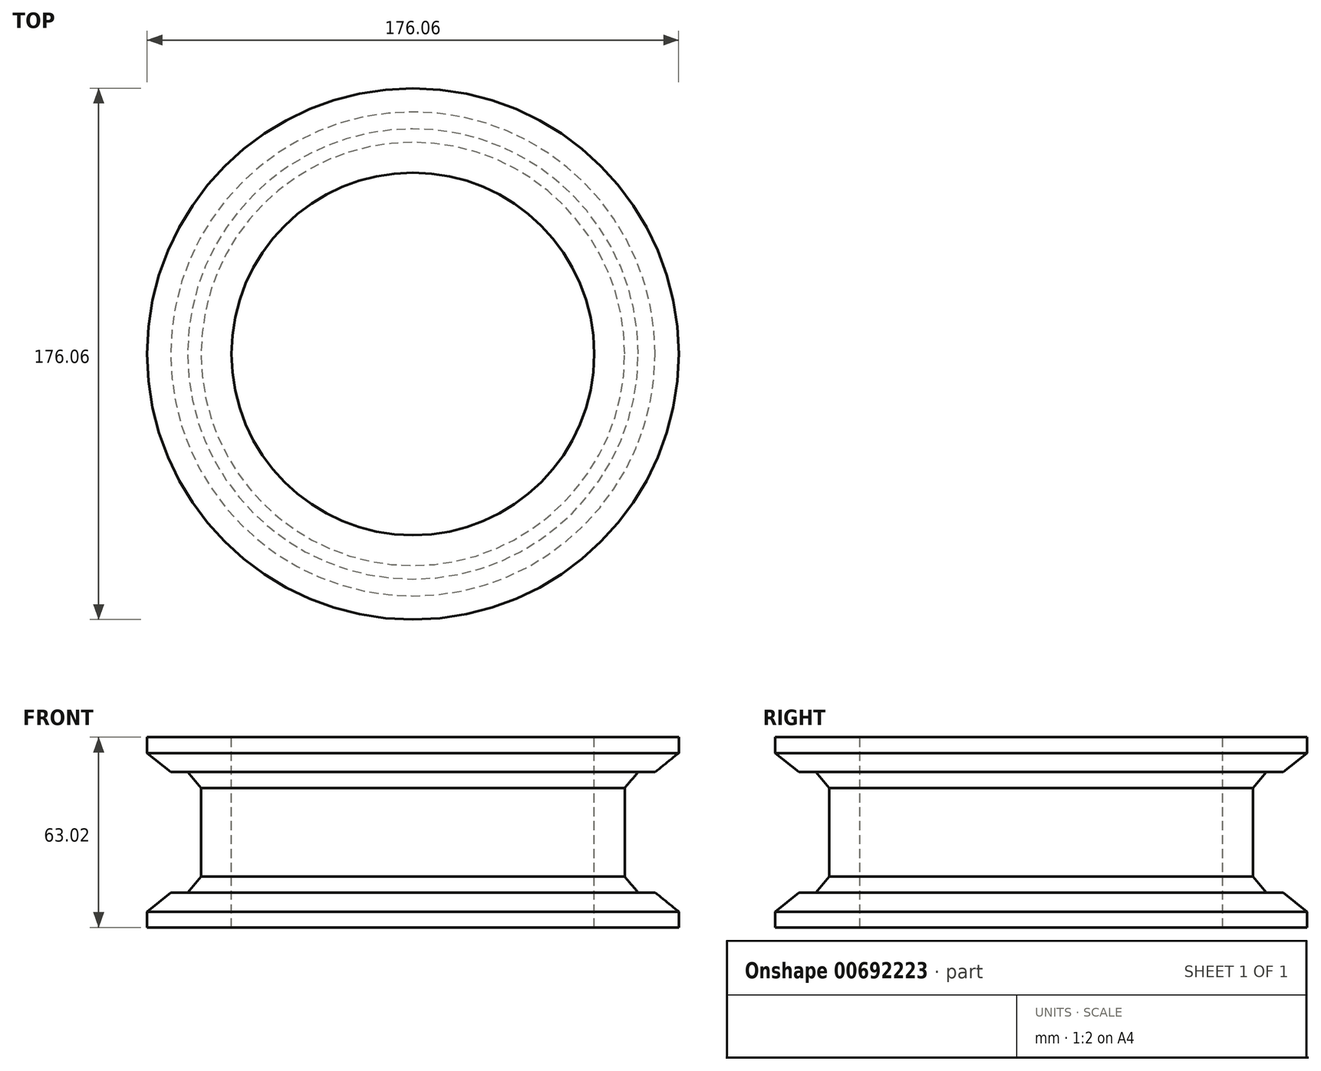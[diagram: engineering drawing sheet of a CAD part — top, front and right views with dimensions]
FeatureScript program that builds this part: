
annotation { "Feature Type Name" : "Feature", "Feature Type Description" : "" }
export const myFeature = defineFeature(function(context is Context, id is Id, definition is map)
    precondition{}
    {
        {
            var Q0;
            Q0=qCreatedBy(makeId("Front.planeOp"),FACE);
            var sketch = newSketch(context, id + "F0", { "sketchPlane" : qUnion([Q0])});
            skLineSegment(sketch, "E0", {"start": v(0, 0) * mm, "end": v(0, -31.5) * mm});
            skLineSegment(sketch, "E1", {"start": v(0, -31.5) * mm, "end": v(-88.03, -31.5) * mm});
            skLineSegment(sketch, "E2", {"start": v(-88.03, -31.5) * mm, "end": v(-88.03, -26.29) * mm});
            skLineSegment(sketch, "E3", {"start": v(-88.03, -26.29) * mm, "end": v(-80.2, -19.95) * mm});
            skLineSegment(sketch, "E4", {"start": v(-80.2, -19.95) * mm, "end": v(-74.6, -19.95) * mm});
            skLineSegment(sketch, "E5", {"start": v(-74.6, -19.95) * mm, "end": v(-70.13, -14.73) * mm});
            skLineSegment(sketch, "E6", {"start": v(-70.13, -14.73) * mm, "end": v(-70.13, 0) * mm});
            skLineSegment(sketch, "E7", {"start": v(-70.13, 0) * mm, "end": v(0, 0) * mm});
            skPoint(sketch, "E8.orphan", {"position": v(0, 21.81) * mm});
            skSolve(sketch);
        }
        {
            var Q0;
            Q0 = qSketchRegion(id + "F0", true);
            var Q1;
            Q1=sQuery(id+"F0.wireOp",EDGE,"E0");
            revolve(context, id + "F1", {"entities" : qUnion([Q0]), "axis" : qUnion([Q1]), "revolveType" : RevolveType.FULL});
        }
        {
            var Q0;
            Q0=makeQuery(id+"F1.opRevolve","SWEPT_BODY",BODY,{"disambiguationData":[OSD([sQuery(id+"F0.wireOp",EDGE,"E0"),sQuery(id+"F0.wireOp",EDGE,"E1"),sQuery(id+"F0.wireOp",EDGE,"E2"),sQuery(id+"F0.wireOp",EDGE,"E3"),sQuery(id+"F0.wireOp",EDGE,"E4"),sQuery(id+"F0.wireOp",EDGE,"E5"),sQuery(id+"F0.wireOp",EDGE,"E6"),sQuery(id+"F0.wireOp",EDGE,"E7")])]});
            var Q1;
            Q1=makeQuery(id+"F1.opRevolve","SWEPT_FACE",FACE,{"disambiguationData":[OSD([sQuery(id+"F0.wireOp",EDGE,"E7")])]});
            mirror(context, id + "F2", {"operationType" : NewBodyOperationType.ADD, "entities" : qUnion([Q0]), "mirrorPlane" : qUnion([Q1])});
        }
        {
            var Q0;
            Q0=makeQuery(id+"F2.opPattern","COPY",FACE,{"derivedFrom":makeQuery(id+"F1.opRevolve","SWEPT_FACE",FACE,{"disambiguationData":[OSD([sQuery(id+"F0.wireOp",EDGE,"E1")])]}),"instanceName":"1"});
            var sketch = newSketch(context, id + "F3", { "sketchPlane" : qUnion([Q0])});
            skCircle(sketch, "E9", {"center": v(0, 0) * mm, "radius": 60.07 * mm});
            skSolve(sketch);
        }
        {
            var Q0;
            Q0 = qSketchRegion(id + "F3", true);
            extrude(context, id + "F4", {"entities" : qUnion([Q0]), "operationType" : NewBodyOperationType.REMOVE, "oppositeDirection" : true, "depth" : 139 * mm, "offsetDistance" : 25 * mm});
        }
    });
